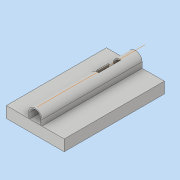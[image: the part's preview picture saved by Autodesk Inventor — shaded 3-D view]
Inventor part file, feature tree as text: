
AUTODESK INVENTOR PART (.ipt)
format: ipt  version: 2019 (Build 230136000, 136)  size: 143,872 bytes
history: native  units: mm
features: other x3, extrude x3, projected_geometry x1
ambient origin geometry x8: Origin, YZ Plane, XZ Plane, XY Plane, X Axis, Y Axis, Z Axis, Center Point
bodies: Body1 (feature_tree)
feature tree (7):
  other  "эскиз_корпус"
  extrude  "корпус_общий"  Depth=5.0mm
  extrude  "отверстие_ручка"  Depth=5.0mm
  extrude  "отверстие_цилиндр"  Depth=1.0mm
  other  "РабОсь1"
  other  "эскиз_отверстие_ручка"
  projected_geometry  "Спроецированная петля6"
